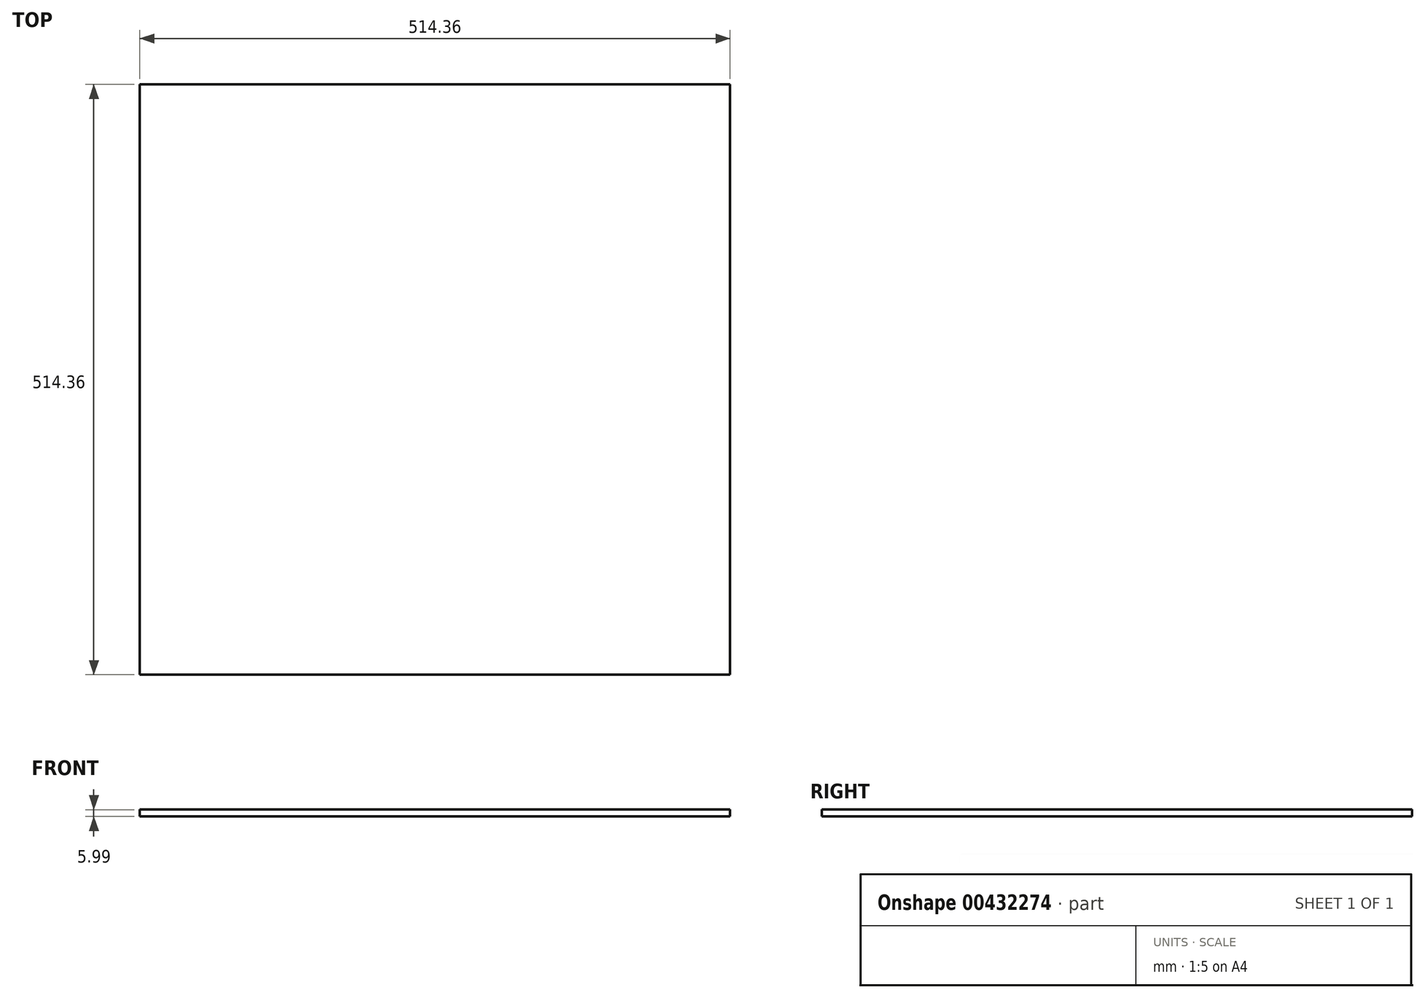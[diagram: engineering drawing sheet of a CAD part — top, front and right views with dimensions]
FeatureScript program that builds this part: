
annotation { "Feature Type Name" : "Feature", "Feature Type Description" : "" }
export const myFeature = defineFeature(function(context is Context, id is Id, definition is map)
    precondition{}
    {
        {
            var Q0;
            Q0=qCreatedBy(makeId("Top.planeOp"),FACE);
            var sketch = newSketch(context, id + "F0", { "sketchPlane" : qUnion([Q0])});
            skLineSegment(sketch, "E0.bottom", {"start": v(-257.18, 257.18) * mm, "end": v(257.18, 257.18) * mm});
            skLineSegment(sketch, "E0.top", {"start": v(-257.18, -257.18) * mm, "end": v(257.18, -257.18) * mm});
            skLineSegment(sketch, "E0.left", {"start": v(-257.18, 257.18) * mm, "end": v(-257.18, -257.18) * mm});
            skLineSegment(sketch, "E0.right", {"start": v(257.18, 257.18) * mm, "end": v(257.18, -257.18) * mm});
            skPoint(sketch, "E0.middle", {"position": v(0, 0) * mm});
            skSolve(sketch);
        }
        {
            var Q0;
            Q0 = qSketchRegion(id + "F0", true);
            extrude(context, id + "F1", {"entities" : qUnion([Q0]), "depth" : 6 * mm, "offsetDistance" : 25.4 * mm});
        }
    });
